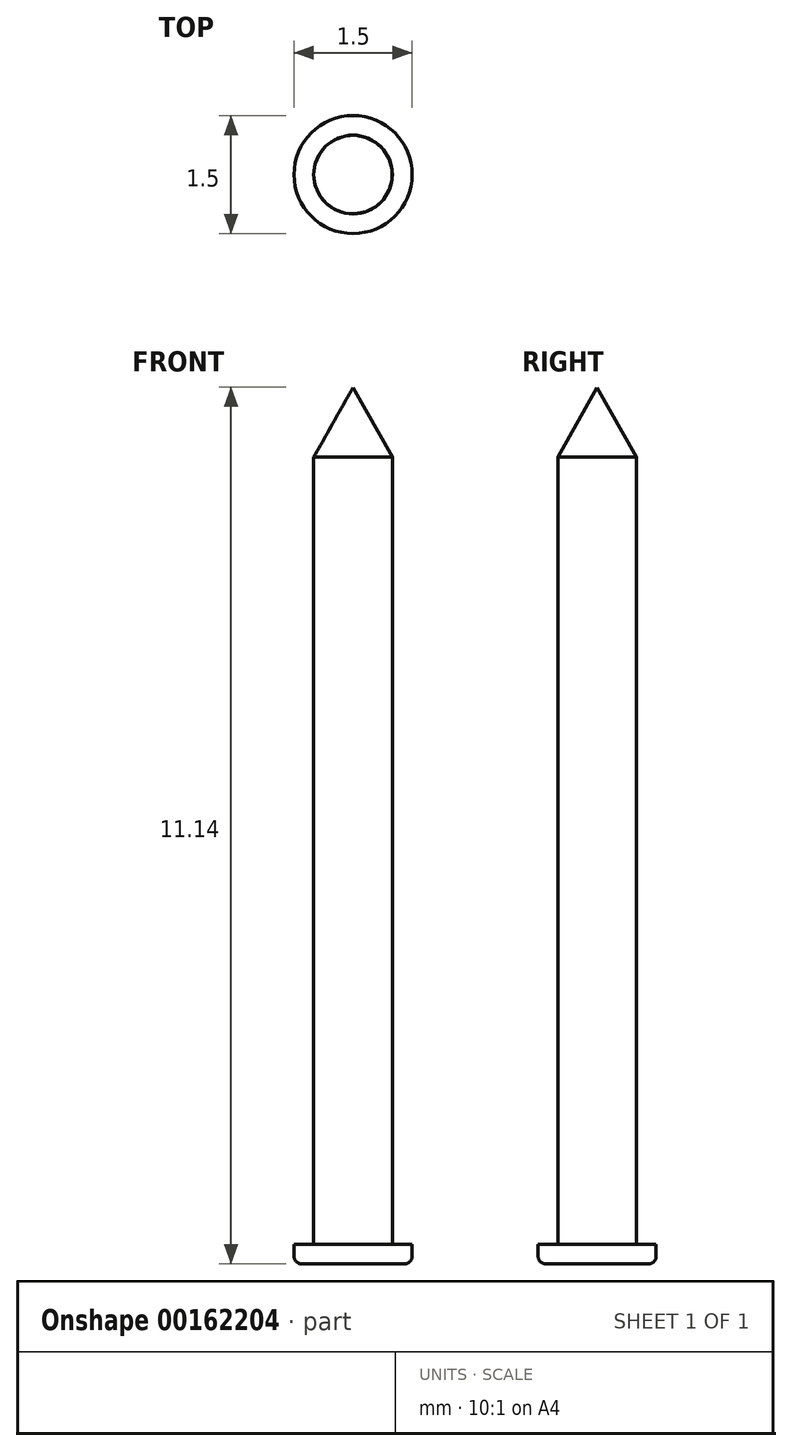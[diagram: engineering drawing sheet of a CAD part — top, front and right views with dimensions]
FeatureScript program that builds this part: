
annotation { "Feature Type Name" : "Feature", "Feature Type Description" : "" }
export const myFeature = defineFeature(function(context is Context, id is Id, definition is map)
    precondition{}
    {
        {
            var Q0;
            Q0=qCreatedBy(makeId("Top.planeOp"),FACE);
            var sketch = newSketch(context, id + "F0", { "sketchPlane" : qUnion([Q0])});
            skCircle(sketch, "E0", {"center": v(0, 0) * mm, "radius": 0.5 * mm});
            skCircle(sketch, "E1", {"center": v(0, 0) * mm, "radius": 0.75 * mm});
            skSolve(sketch);
        }
        {
            var Q0;
            Q0=makeQuery(id+"F0.imprint","IMPRINT",FACE,{"disambiguationData":[TD([[makeQuery(id+"F0.imprint","IMPRINT",EDGE,{"derivedFrom":sQuery(id+"F0.wireOp",EDGE,"E0")}),1.0]])]});
            extrude(context, id + "F1", {"entities" : qUnion([Q0]), "depth" : 10 * mm});
        }
        {
            var Q0;
            Q0=makeQuery(id+"F0.imprint","IMPRINT",FACE,{"disambiguationData":[TD([[makeQuery(id+"F0.imprint","IMPRINT",EDGE,{"derivedFrom":sQuery(id+"F0.wireOp",EDGE,"E0")}),-1.0]])]});
            var Q1;
            Q1=makeQuery(id+"F0.imprint","IMPRINT",FACE,{"disambiguationData":[TD([[makeQuery(id+"F0.imprint","IMPRINT",EDGE,{"derivedFrom":sQuery(id+"F0.wireOp",EDGE,"E0")}),1.0]])]});
            extrude(context, id + "F2", {"entities" : qUnion([Q0, Q1]), "operationType" : NewBodyOperationType.ADD, "oppositeDirection" : true, "depth" : .25 * mm});
        }
        {
            var Q0;
            Q0=makeQuery(id+"F2.opExtrude","CAP_EDGE",EDGE,{"disambiguationData":[OSD([sQuery(id+"F0.wireOp",EDGE,"E1")])],"isStart":false});
            fillet(context, id + "F3", {"entities" : qUnion([Q0]), "radius" : .1 * mm, "tangentPropagation" : true, "allowEdgeOverflow" : false});
        }
        {
            var Q0;
            Q0=qCreatedBy(makeId("Front.planeOp"),FACE);
            var sketch = newSketch(context, id + "F4", { "sketchPlane" : qUnion([Q0])});
            skLineSegment(sketch, "E2", {"start": v(0, 10.89) * mm, "end": v(0.5, 10) * mm});
            skLineSegment(sketch, "E3", {"start": v(0.5, 10) * mm, "end": v(0, 10) * mm});
            skLineSegment(sketch, "E4", {"start": v(0, 10) * mm, "end": v(0, 10.89) * mm});
            skSolve(sketch);
        }
        {
            var Q0;
            Q0=makeQuery(id+"F4.imprint","IMPRINT",FACE,{"disambiguationData":[TD([[makeQuery(id+"F4.imprint","IMPRINT",EDGE,{"derivedFrom":sQuery(id+"F4.wireOp",EDGE,"E2")}),-1.0]])]});
            var Q1;
            Q1=sQuery(id+"F4.wireOp",EDGE,"E4");
            revolve(context, id + "F5", {"operationType" : NewBodyOperationType.ADD, "entities" : qUnion([Q0]), "axis" : qUnion([Q1]), "revolveType" : RevolveType.FULL});
        }
    });
